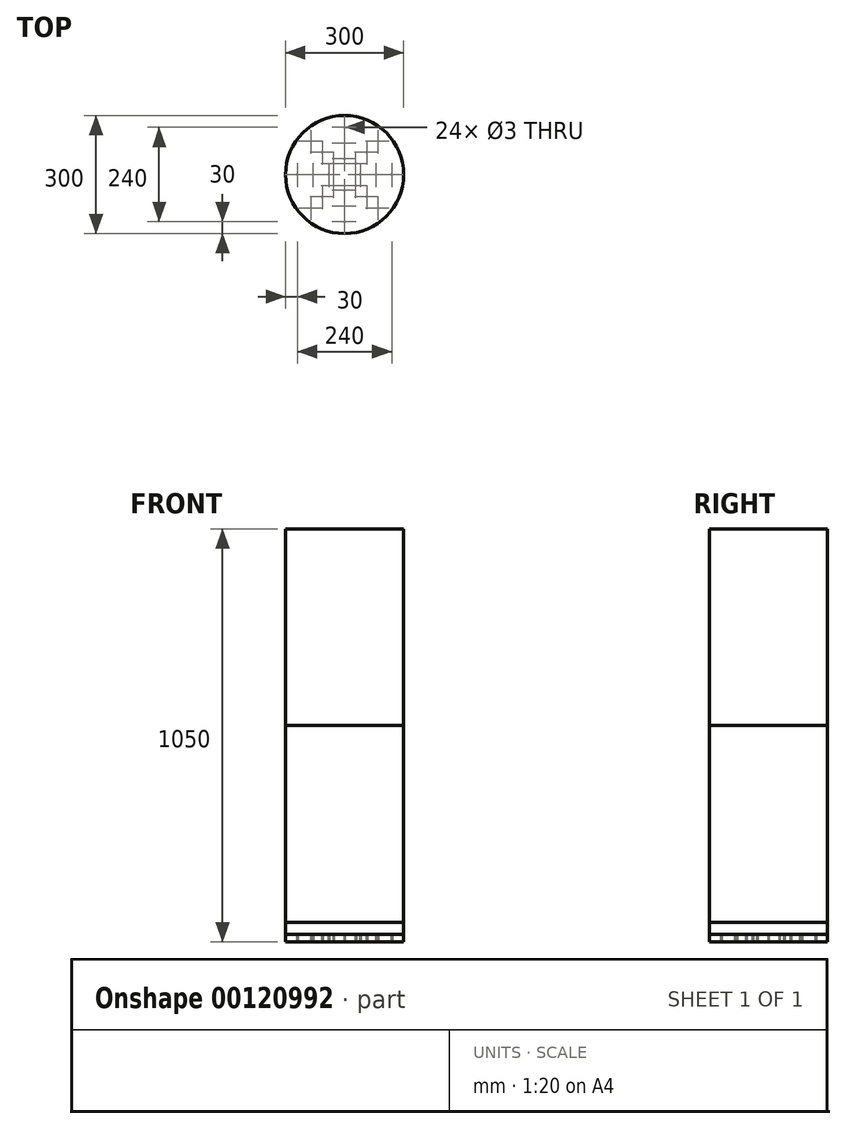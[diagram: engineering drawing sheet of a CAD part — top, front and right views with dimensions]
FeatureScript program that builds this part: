
annotation { "Feature Type Name" : "Feature", "Feature Type Description" : "" }
export const myFeature = defineFeature(function(context is Context, id is Id, definition is map)
    precondition{}
    {
        {
            var Q0;
            Q0=qCreatedBy(makeId("Top.planeOp"),FACE);
            var sketch = newSketch(context, id + "F0", { "sketchPlane" : qUnion([Q0])});
            skCircle(sketch, "E0", {"center": v(0, 0) * mm, "radius": 150 * mm});
            skCircle(sketch, "E1", {"center": v(0, 40) * mm, "radius": 1.5 * mm});
            skCircle(sketch, "E2", {"center": v(0, 80) * mm, "radius": 1.5 * mm});
            skCircle(sketch, "E3", {"center": v(0, 120) * mm, "radius": 1.5 * mm});
            skCircle(sketch, "E4.1.0", {"center": v(56.57, 56.57) * mm, "radius": 1.5 * mm});
            skCircle(sketch, "E4.1.1", {"center": v(84.85, 84.85) * mm, "radius": 1.5 * mm});
            skCircle(sketch, "E4.1.2", {"center": v(28.28, 28.28) * mm, "radius": 1.5 * mm});
            skCircle(sketch, "E4.2.0", {"center": v(80, 0) * mm, "radius": 1.5 * mm});
            skCircle(sketch, "E4.2.1", {"center": v(120, 0) * mm, "radius": 1.5 * mm});
            skCircle(sketch, "E4.2.2", {"center": v(40, 0) * mm, "radius": 1.5 * mm});
            skCircle(sketch, "E4.3.0", {"center": v(56.57, -56.57) * mm, "radius": 1.5 * mm});
            skCircle(sketch, "E4.3.1", {"center": v(84.85, -84.85) * mm, "radius": 1.5 * mm});
            skCircle(sketch, "E4.3.2", {"center": v(28.28, -28.28) * mm, "radius": 1.5 * mm});
            skCircle(sketch, "E4.4.0", {"center": v(0, -80) * mm, "radius": 1.5 * mm});
            skCircle(sketch, "E4.4.1", {"center": v(0, -120) * mm, "radius": 1.5 * mm});
            skCircle(sketch, "E4.4.2", {"center": v(0, -40) * mm, "radius": 1.5 * mm});
            skCircle(sketch, "E4.5.0", {"center": v(-56.57, -56.57) * mm, "radius": 1.5 * mm});
            skCircle(sketch, "E4.5.1", {"center": v(-84.85, -84.85) * mm, "radius": 1.5 * mm});
            skCircle(sketch, "E4.5.2", {"center": v(-28.28, -28.28) * mm, "radius": 1.5 * mm});
            skCircle(sketch, "E4.6.0", {"center": v(-80, 0) * mm, "radius": 1.5 * mm});
            skCircle(sketch, "E4.6.1", {"center": v(-120, 0) * mm, "radius": 1.5 * mm});
            skCircle(sketch, "E4.6.2", {"center": v(-40, 0) * mm, "radius": 1.5 * mm});
            skCircle(sketch, "E4.7.0", {"center": v(-56.57, 56.57) * mm, "radius": 1.5 * mm});
            skCircle(sketch, "E4.7.1", {"center": v(-84.85, 84.85) * mm, "radius": 1.5 * mm});
            skCircle(sketch, "E4.7.2", {"center": v(-28.28, 28.28) * mm, "radius": 1.5 * mm});
            skSolve(sketch);
        }
        {
            var Q0;
            Q0 = qSketchRegion(id + "F0", true);
            extrude(context, id + "F1", {"entities" : qUnion([Q0]), "depth" : 20 * mm});
        }
        {
            var Q0;
            Q0=makeQuery(id+"F1.opExtrude","CAP_FACE",FACE,{"disambiguationData":[OSD([sQuery(id+"F0.wireOp",EDGE,"E0"),sQuery(id+"F0.wireOp",EDGE,"E4.1.0"),sQuery(id+"F0.wireOp",EDGE,"E4.1.1"),sQuery(id+"F0.wireOp",EDGE,"E4.1.2"),sQuery(id+"F0.wireOp",EDGE,"E4.2.0"),sQuery(id+"F0.wireOp",EDGE,"E4.2.1"),sQuery(id+"F0.wireOp",EDGE,"E4.2.2"),sQuery(id+"F0.wireOp",EDGE,"E4.3.0"),sQuery(id+"F0.wireOp",EDGE,"E4.3.1"),sQuery(id+"F0.wireOp",EDGE,"E4.3.2"),sQuery(id+"F0.wireOp",EDGE,"E4.4.0"),sQuery(id+"F0.wireOp",EDGE,"E4.4.1"),sQuery(id+"F0.wireOp",EDGE,"E4.4.2"),sQuery(id+"F0.wireOp",EDGE,"E4.5.0"),sQuery(id+"F0.wireOp",EDGE,"E4.5.1"),sQuery(id+"F0.wireOp",EDGE,"E4.5.2"),sQuery(id+"F0.wireOp",EDGE,"E4.6.0"),sQuery(id+"F0.wireOp",EDGE,"E4.6.1"),sQuery(id+"F0.wireOp",EDGE,"E4.6.2"),sQuery(id+"F0.wireOp",EDGE,"E4.7.0"),sQuery(id+"F0.wireOp",EDGE,"E4.7.1"),sQuery(id+"F0.wireOp",EDGE,"E4.7.2"),sQuery(id+"F0.wireOp",EDGE,"E2"),sQuery(id+"F0.wireOp",EDGE,"E3"),sQuery(id+"F0.wireOp",EDGE,"E1")])],"isStart":false});
            var sketch = newSketch(context, id + "F2", { "sketchPlane" : qUnion([Q0])});
            skCircle(sketch, "E5", {"center": v(0, 0) * mm, "radius": 150 * mm});
            skSolve(sketch);
        }
        {
            var Q0;
            Q0 = qSketchRegion(id + "F2", true);
            extrude(context, id + "F3", {"entities" : qUnion([Q0]), "depth" : 30 * mm});
        }
        {
            var Q0;
            Q0=makeQuery(id+"F3.opExtrude","CAP_FACE",FACE,{"disambiguationData":[OSD([sQuery(id+"F2.wireOp",EDGE,"E5")])],"isStart":false});
            var sketch = newSketch(context, id + "F4", { "sketchPlane" : qUnion([Q0])});
            skCircle(sketch, "E6", {"center": v(0, 0) * mm, "radius": 150 * mm});
            skSolve(sketch);
        }
        {
            var Q0;
            Q0 = qSketchRegion(id + "F4", true);
            extrude(context, id + "F5", {"entities" : qUnion([Q0]), "depth" : 500 * mm});
        }
        {
            var Q0;
            Q0=makeQuery(id+"F5.opExtrude","CAP_FACE",FACE,{"disambiguationData":[OSD([sQuery(id+"F4.wireOp",EDGE,"E6")])],"isStart":false});
            var sketch = newSketch(context, id + "F6", { "sketchPlane" : qUnion([Q0])});
            skCircle(sketch, "E7", {"center": v(0, 0) * mm, "radius": 150 * mm});
            skSolve(sketch);
        }
        {
            var Q0;
            Q0 = qSketchRegion(id + "F6", true);
            extrude(context, id + "F7", {"entities" : qUnion([Q0]), "depth" : 500 * mm});
        }
    });
